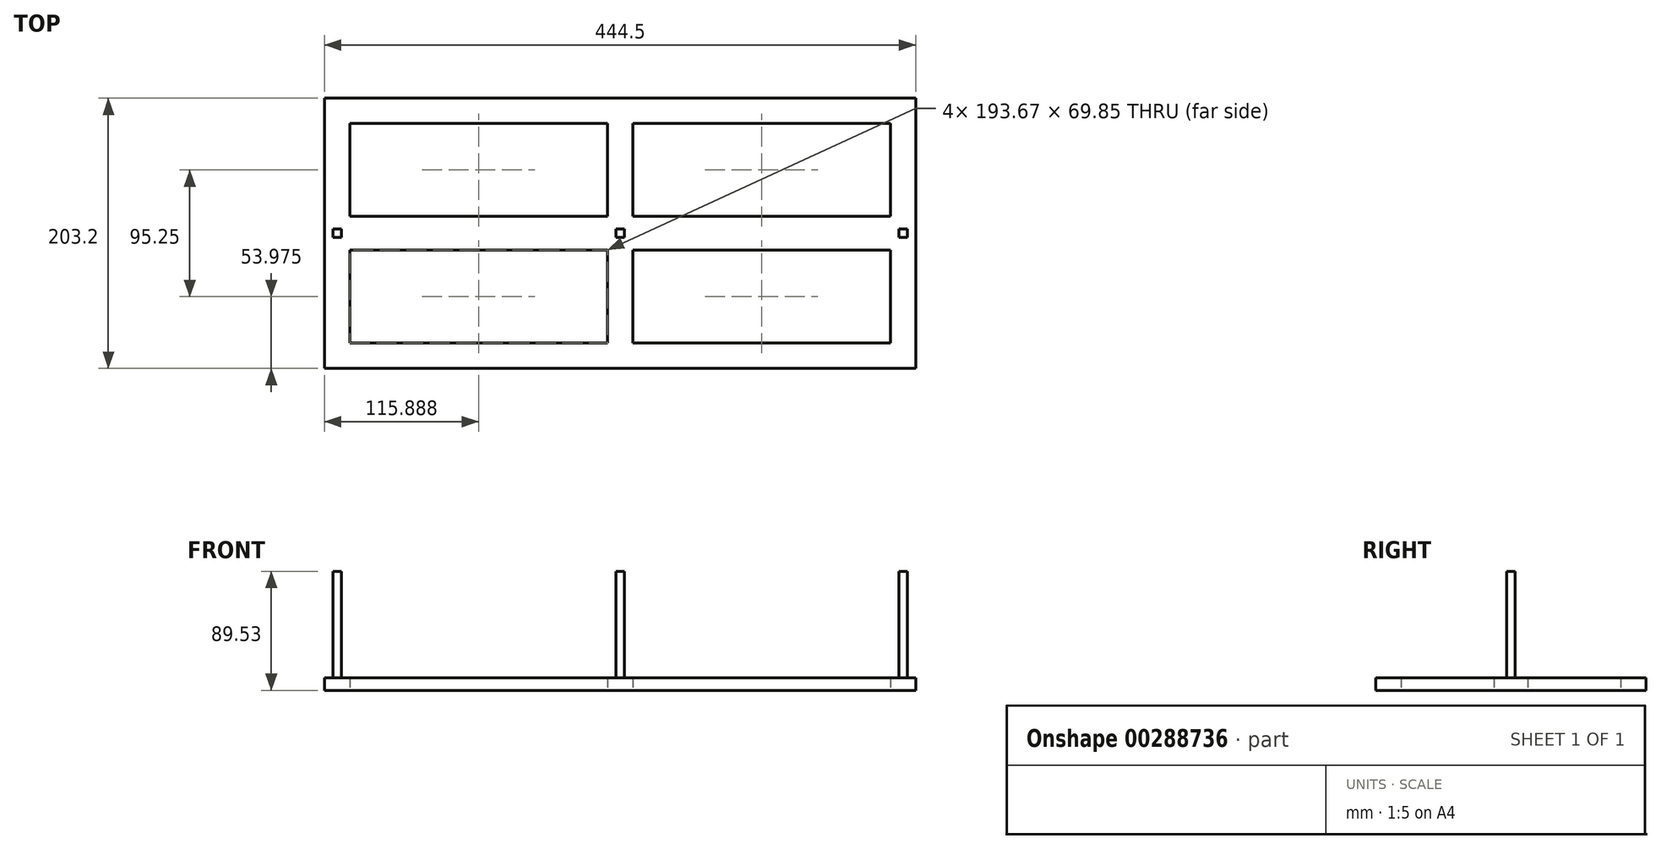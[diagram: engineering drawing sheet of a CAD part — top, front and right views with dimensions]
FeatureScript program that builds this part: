
annotation { "Feature Type Name" : "Feature", "Feature Type Description" : "" }
export const myFeature = defineFeature(function(context is Context, id is Id, definition is map)
    precondition{}
    {
        {
            var Q0;
            Q0=qCreatedBy(makeId("Top.planeOp"),FACE);
            var sketch = newSketch(context, id + "F0", { "sketchPlane" : qUnion([Q0])});
            skLineSegment(sketch, "E0.bottom", {"start": v(222.25, 101.6) * mm, "end": v(-222.25, 101.6) * mm});
            skLineSegment(sketch, "E0.top", {"start": v(222.25, -101.6) * mm, "end": v(-222.25, -101.6) * mm});
            skLineSegment(sketch, "E0.left", {"start": v(222.25, 101.6) * mm, "end": v(222.25, -101.6) * mm});
            skLineSegment(sketch, "E0.right", {"start": v(-222.25, 101.6) * mm, "end": v(-222.25, -101.6) * mm});
            skPoint(sketch, "E0.middle", {"position": v(0, 0) * mm});
            skLineSegment(sketch, "E1", {"start": v(218, 0) * mm, "end": v(-272.7, 0) * mm, "construction": true});
            skLineSegment(sketch, "E2", {"start": v(0, 217.92) * mm, "end": v(0, -210.13) * mm, "construction": true});
            skLineSegment(sketch, "E3", {"start": v(-9.52, 82.55) * mm, "end": v(-9.52, 12.7) * mm});
            skLineSegment(sketch, "E4", {"start": v(203.2, 12.7) * mm, "end": v(9.53, 12.7) * mm});
            skLineSegment(sketch, "E5.MirrorCS", {"start": v(9.53, 82.55) * mm, "end": v(9.53, 12.7) * mm});
            skLineSegment(sketch, "E6.MirrorCS", {"start": v(203.2, -12.7) * mm, "end": v(9.53, -12.7) * mm});
            skLineSegment(sketch, "E7.0", {"start": v(203.2, 82.55) * mm, "end": v(9.53, 82.55) * mm});
            skLineSegment(sketch, "E7.1", {"start": v(203.2, 82.55) * mm, "end": v(203.2, 12.7) * mm});
            skLineSegment(sketch, "E7.2", {"start": v(203.2, -82.55) * mm, "end": v(9.53, -82.55) * mm});
            skLineSegment(sketch, "E7.3", {"start": v(-203.2, 82.55) * mm, "end": v(-203.2, 12.7) * mm});
            skPoint(sketch, "E8.orphan", {"position": v(9.53, -101.6) * mm});
            skPoint(sketch, "E9.orphan", {"position": v(-9.52, -101.6) * mm});
            skLineSegment(sketch, "E10.trimOffspring", {"start": v(-9.52, -82.55) * mm, "end": v(-203.2, -82.55) * mm});
            skLineSegment(sketch, "E11.trimOffspring", {"start": v(203.2, -12.7) * mm, "end": v(203.2, -82.55) * mm});
            skPoint(sketch, "E12.orphan", {"position": v(222.25, -12.7) * mm});
            skPoint(sketch, "E13.orphan", {"position": v(222.25, 12.7) * mm});
            skLineSegment(sketch, "E14.trimOffspring", {"start": v(-9.52, -12.7) * mm, "end": v(-9.52, -82.55) * mm});
            skLineSegment(sketch, "E15.trimOffspring", {"start": v(-9.52, 12.7) * mm, "end": v(-203.2, 12.7) * mm});
            skLineSegment(sketch, "E16.trimOffspring", {"start": v(9.53, -12.7) * mm, "end": v(9.53, -82.55) * mm});
            skLineSegment(sketch, "E17.trimOffspring", {"start": v(-9.52, -12.7) * mm, "end": v(-203.2, -12.7) * mm});
            skLineSegment(sketch, "E18.trimOffspring", {"start": v(-9.52, -12.7) * mm, "end": v(-222.25, -12.7) * mm});
            skLineSegment(sketch, "E19.trimOffspring", {"start": v(-203.2, -12.7) * mm, "end": v(-203.2, -82.55) * mm});
            skPoint(sketch, "E20.orphan", {"position": v(-222.25, 12.7) * mm});
            skPoint(sketch, "E21.orphan", {"position": v(-222.25, -12.7) * mm});
            skPoint(sketch, "E22.orphan", {"position": v(-9.52, 101.6) * mm});
            skLineSegment(sketch, "E23.trimOffspring", {"start": v(-9.52, 82.55) * mm, "end": v(-203.2, 82.55) * mm});
            skPoint(sketch, "E24.orphan", {"position": v(9.53, 101.6) * mm});
            skSolve(sketch);
        }
        {
            var Q0;
            Q0 = qSketchRegion(id + "F0", true);
            extrude(context, id + "F1", {"entities" : qUnion([Q0]), "depth" : 9.52 * mm});
        }
        {
            var Q0;
            Q0=makeQuery(id+"F1.opExtrude","CAP_FACE",FACE,{"disambiguationData":[OSD([sQuery(id+"F0.wireOp",EDGE,"E0.bottom"),sQuery(id+"F0.wireOp",EDGE,"E0.top"),sQuery(id+"F0.wireOp",EDGE,"E0.left"),sQuery(id+"F0.wireOp",EDGE,"E0.right"),sQuery(id+"F0.wireOp",EDGE,"E3"),sQuery(id+"F0.wireOp",EDGE,"E4"),sQuery(id+"F0.wireOp",EDGE,"E5.MirrorCS"),sQuery(id+"F0.wireOp",EDGE,"E6.MirrorCS"),sQuery(id+"F0.wireOp",EDGE,"E7.0"),sQuery(id+"F0.wireOp",EDGE,"E7.1"),sQuery(id+"F0.wireOp",EDGE,"E7.2"),sQuery(id+"F0.wireOp",EDGE,"E7.3"),sQuery(id+"F0.wireOp",EDGE,"E10.trimOffspring"),sQuery(id+"F0.wireOp",EDGE,"E11.trimOffspring"),sQuery(id+"F0.wireOp",EDGE,"E14.trimOffspring"),sQuery(id+"F0.wireOp",EDGE,"E15.trimOffspring"),sQuery(id+"F0.wireOp",EDGE,"E16.trimOffspring"),sQuery(id+"F0.wireOp",EDGE,"E18.trimOffspring"),sQuery(id+"F0.wireOp",EDGE,"E19.trimOffspring"),sQuery(id+"F0.wireOp",EDGE,"E23.trimOffspring")])],"isStart":false});
            var sketch = newSketch(context, id + "F2", { "sketchPlane" : qUnion([Q0])});
            skLineSegment(sketch, "E25.bottom", {"start": v(209.55, 3.17) * mm, "end": v(215.9, 3.17) * mm});
            skLineSegment(sketch, "E25.top", {"start": v(209.55, -3.18) * mm, "end": v(215.9, -3.18) * mm});
            skLineSegment(sketch, "E25.left", {"start": v(209.55, 3.17) * mm, "end": v(209.55, -3.18) * mm});
            skLineSegment(sketch, "E25.right", {"start": v(215.9, 3.17) * mm, "end": v(215.9, -3.18) * mm});
            skPoint(sketch, "E25.middle", {"position": v(212.73, 0) * mm});
            skLineSegment(sketch, "E26.bottom", {"start": v(-209.55, 3.18) * mm, "end": v(-215.9, 3.18) * mm});
            skLineSegment(sketch, "E26.top", {"start": v(-209.55, -3.18) * mm, "end": v(-215.9, -3.17) * mm});
            skLineSegment(sketch, "E26.left", {"start": v(-209.55, 3.17) * mm, "end": v(-209.55, -3.17) * mm});
            skLineSegment(sketch, "E26.right", {"start": v(-215.9, 3.18) * mm, "end": v(-215.9, -3.17) * mm});
            skPoint(sketch, "E26.middle", {"position": v(-212.73, 0) * mm});
            skLineSegment(sketch, "E27.bottom", {"start": v(3.18, 3.17) * mm, "end": v(-3.18, 3.18) * mm});
            skLineSegment(sketch, "E27.top", {"start": v(3.17, -3.18) * mm, "end": v(-3.18, -3.17) * mm});
            skLineSegment(sketch, "E27.left", {"start": v(3.18, 3.17) * mm, "end": v(3.18, -3.18) * mm});
            skLineSegment(sketch, "E27.right", {"start": v(-3.17, 3.18) * mm, "end": v(-3.18, -3.17) * mm});
            skPoint(sketch, "E27.middle", {"position": v(0, 0) * mm});
            skSolve(sketch);
        }
        {
            var Q0;
            Q0=makeQuery(id+"F2.imprint","IMPRINT",FACE,{"disambiguationData":[TD([[makeQuery(id+"F2.imprint","IMPRINT",EDGE,{"derivedFrom":sQuery(id+"F2.wireOp",EDGE,"E26.bottom")}),1.0]])]});
            var Q1;
            Q1=makeQuery(id+"F2.imprint","IMPRINT",FACE,{"disambiguationData":[TD([[makeQuery(id+"F2.imprint","IMPRINT",EDGE,{"derivedFrom":sQuery(id+"F2.wireOp",EDGE,"E25.bottom")}),-1.0]])]});
            var Q2;
            Q2=makeQuery(id+"F2.imprint","IMPRINT",FACE,{"disambiguationData":[TD([[makeQuery(id+"F2.imprint","IMPRINT",EDGE,{"derivedFrom":sQuery(id+"F2.wireOp",EDGE,"E27.bottom")}),1.0]])]});
            extrude(context, id + "F3", {"entities" : qUnion([Q0, Q1, Q2]), "operationType" : NewBodyOperationType.ADD, "depth" : 2.54 * mm});
        }
        {
            var Q0;
            Q0=makeQuery(id+"F3.opExtrude","CAP_FACE",FACE,{"disambiguationData":[OSD([sQuery(id+"F2.wireOp",EDGE,"E27.bottom"),sQuery(id+"F2.wireOp",EDGE,"E27.top"),sQuery(id+"F2.wireOp",EDGE,"E27.left"),sQuery(id+"F2.wireOp",EDGE,"E27.right")])],"isStart":false});
            var sketch = newSketch(context, id + "F4", { "sketchPlane" : qUnion([Q0])});
            skCircle(sketch, "E28", {"center": v(0, 0) * mm, "radius": 3.18 * mm, "construction": true});
            skLineSegment(sketch, "E29.bottom", {"start": v(3.18, 3.18) * mm, "end": v(-3.18, 3.18) * mm});
            skLineSegment(sketch, "E29.top", {"start": v(3.18, -3.18) * mm, "end": v(-3.18, -3.18) * mm});
            skLineSegment(sketch, "E29.left", {"start": v(3.18, 3.18) * mm, "end": v(3.18, -3.17) * mm});
            skLineSegment(sketch, "E29.right", {"start": v(-3.18, 3.18) * mm, "end": v(-3.18, -3.17) * mm});
            skLineSegment(sketch, "E30.bottom", {"start": v(215.9, -3.17) * mm, "end": v(209.55, -3.17) * mm});
            skLineSegment(sketch, "E30.top", {"start": v(215.9, 3.18) * mm, "end": v(209.55, 3.18) * mm});
            skLineSegment(sketch, "E30.left", {"start": v(215.9, -3.17) * mm, "end": v(215.9, 3.18) * mm});
            skLineSegment(sketch, "E30.right", {"start": v(209.55, -3.17) * mm, "end": v(209.55, 3.18) * mm});
            skPoint(sketch, "E30.middle", {"position": v(212.73, 0) * mm});
            skLineSegment(sketch, "E31.bottom", {"start": v(-209.55, 3.17) * mm, "end": v(-215.9, 3.17) * mm});
            skLineSegment(sketch, "E31.top", {"start": v(-209.55, -3.18) * mm, "end": v(-215.9, -3.18) * mm});
            skLineSegment(sketch, "E31.left", {"start": v(-209.55, 3.17) * mm, "end": v(-209.55, -3.18) * mm});
            skLineSegment(sketch, "E31.right", {"start": v(-215.9, 3.17) * mm, "end": v(-215.9, -3.18) * mm});
            skPoint(sketch, "E31.middle", {"position": v(-212.73, 0) * mm});
            skSolve(sketch);
        }
        {
            var Q0;
            Q0 = qSketchRegion(id + "F4", true);
            extrude(context, id + "F5", {"entities" : qUnion([Q0]), "operationType" : NewBodyOperationType.ADD, "depth" : 77.47 * mm});
        }
    });
